# Revit family: PIA-105_RFA
name_source: partatom
category: Aparatos sanitarios
units: mm (PartAtom-declared; Revit-internal decimal feet)

## family parameters
Compartido = No
Corte con vacíos al cargar = No
Cota de conector redondo = Diámetro de uso
Número OmniClass = 23.45.00.00
Punto de cálculo de habitación = No
Se basa en plano de trabajo = No
Siempre vertical = Sí
Tipo de pieza = Normal
Título OmniClass = Sanitary, Laundry, and Cleaning Equipment

## types (1)
- PIA-105
    Brass Chromed = Brass
    Comentarios de tipo = Accesorios: Kit de sujeción para muro falso y sólido.
    Data Sheet = https://helvex.com.mx
    Descripción = Toallero de barra
    Elevación por defecto = 0"
    Fabricante = HELVEX
    Imagen de tipo = PIA-105.png
    Instructive = https://helvex.com.mx
    Modelo = PIA-105
    Total Depth = 2"
    Total Length = 17"
    Total Support Diameter = 2"

## geometry (parser evidence)
native form markers: Sweep x3
no freeform markers — native parametric forms only
